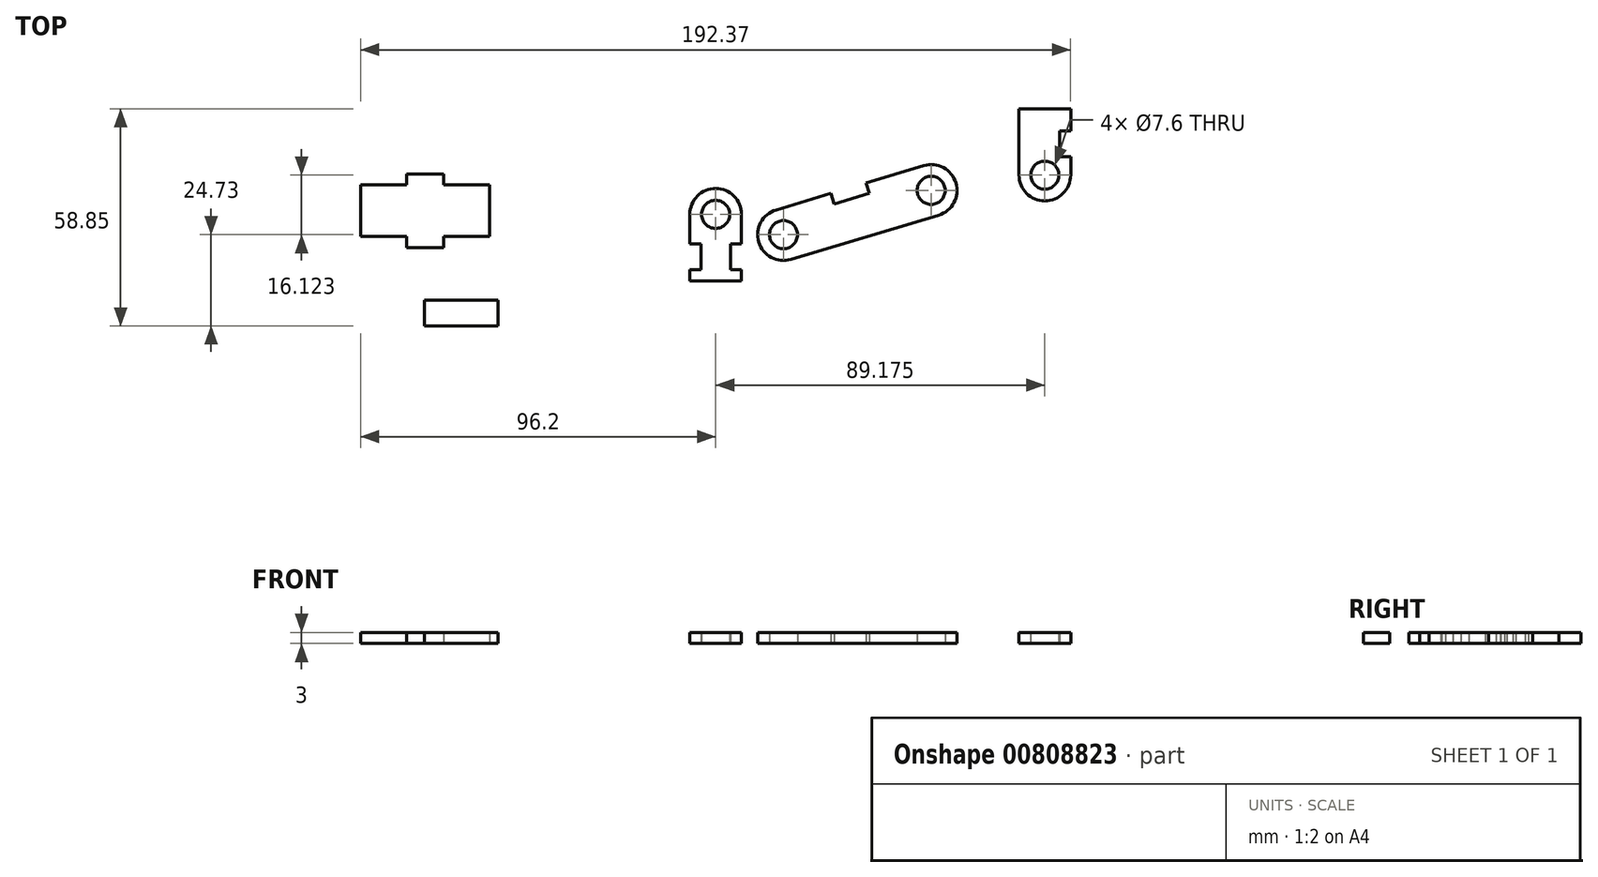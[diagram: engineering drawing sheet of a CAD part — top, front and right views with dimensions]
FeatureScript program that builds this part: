
annotation { "Feature Type Name" : "Feature", "Feature Type Description" : "" }
export const myFeature = defineFeature(function(context is Context, id is Id, definition is map)
    precondition{}
    {
        {
            var Q0;
            Q0=qCreatedBy(makeId("Top.planeOp"),FACE);
            var sketch = newSketch(context, id + "F0", { "sketchPlane" : qUnion([Q0])});
            skLineSegment(sketch, "E0.bottom", {"start": v(-7, 12.5) * mm, "end": v(7, 12.5) * mm});
            skLineSegment(sketch, "E0.top", {"start": v(-7, -12.5) * mm, "end": v(7, -12.5) * mm});
            skLineSegment(sketch, "E0.left", {"start": v(-7, 12.5) * mm, "end": v(-7, -12.5) * mm});
            skLineSegment(sketch, "E0.right", {"start": v(7, 12.5) * mm, "end": v(7, -12.5) * mm});
            skPoint(sketch, "E0.middle", {"position": v(0, 0) * mm});
            skCircle(sketch, "E1", {"center": v(0, 5.5) * mm, "radius": 7 * mm});
            skCircle(sketch, "E2", {"center": v(0, 5.5) * mm, "radius": 3.8 * mm});
            skLineSegment(sketch, "E3.bottom", {"start": v(-7, -9.5) * mm, "end": v(-4, -9.5) * mm});
            skLineSegment(sketch, "E3.top", {"start": v(-7, -2.5) * mm, "end": v(-4, -2.5) * mm});
            skLineSegment(sketch, "E3.left", {"start": v(-7, -9.5) * mm, "end": v(-7, -2.5) * mm});
            skLineSegment(sketch, "E3.right", {"start": v(-4, -9.5) * mm, "end": v(-4, -2.5) * mm});
            skLineSegment(sketch, "E4.bottom", {"start": v(7, -9.5) * mm, "end": v(4, -9.5) * mm});
            skLineSegment(sketch, "E4.top", {"start": v(7, -2.5) * mm, "end": v(4, -2.5) * mm});
            skLineSegment(sketch, "E4.left", {"start": v(7, -9.5) * mm, "end": v(7, -2.5) * mm});
            skLineSegment(sketch, "E4.right", {"start": v(4, -9.5) * mm, "end": v(4, -2.5) * mm});
            skSolve(sketch);
        }
        {
            var Q0;
            {var subQ7=sQuery(id+"F0.wireOp",EDGE,"E0.top");Q0=makeQuery(id+"F0.imprint","IMPRINT",FACE,{"disambiguationData":[TD([[makeQuery(id+"F0.imprint","IMPRINT",EDGE,{"derivedFrom":subQ7}),1.0]])]});}
            var Q1;
            Q1=makeQuery(id+"F0.imprint","IMPRINT",FACE,{"disambiguationData":[TD([[makeQuery(id+"F0.imprint","IMPRINT",EDGE,{"derivedFrom":sQuery(id+"F0.wireOp",EDGE,"E2")}),-1.0]])]});
            extrude(context, id + "F1", {"entities" : qUnion([Q0, Q1]), "depth" : 3 * mm, "offsetDistance" : 25 * mm});
        }
        {
            var Q0;
            Q0=qCreatedBy(makeId("Top.planeOp"),FACE);
            var sketch = newSketch(context, id + "F2", { "sketchPlane" : qUnion([Q0])});
            skLineSegment(sketch, "E5", {"start": v(18.38, 0) * mm, "end": v(58.38, 12) * mm});
            skCircle(sketch, "E6", {"center": v(18.38, 0) * mm, "radius": 7 * mm});
            skCircle(sketch, "E7", {"center": v(58.38, 12) * mm, "radius": 7 * mm});
            skCircle(sketch, "E8", {"center": v(58.38, 12) * mm, "radius": 3.8 * mm});
            skCircle(sketch, "E9", {"center": v(18.38, 0) * mm, "radius": 3.8 * mm});
            skLineSegment(sketch, "E10", {"start": v(16.37, 6.7) * mm, "end": v(56.37, 18.7) * mm});
            skLineSegment(sketch, "E11", {"start": v(60.4, 5.3) * mm, "end": v(20.4, -6.7) * mm});
            skLineSegment(sketch, "E12", {"start": v(31.21, 11.16) * mm, "end": v(32.08, 8.29) * mm});
            skLineSegment(sketch, "E13", {"start": v(32.08, 8.29) * mm, "end": v(41.65, 11.16) * mm});
            skLineSegment(sketch, "E14", {"start": v(41.65, 11.16) * mm, "end": v(40.8, 14.03) * mm});
            skSolve(sketch);
        }
        {
            var Q0;
            {var subQ5=sQuery(id+"F2.wireOp",EDGE,"E11");Q0=makeQuery(id+"F2.imprint","IMPRINT",FACE,{"disambiguationData":[TD([[makeQuery(id+"F2.imprint","IMPRINT",EDGE,{"derivedFrom":subQ5}),-1.0]])]});}
            var Q1;
            Q1=makeQuery(id+"F2.imprint","IMPRINT",FACE,{"disambiguationData":[TD([[makeQuery(id+"F2.imprint","IMPRINT",EDGE,{"derivedFrom":sQuery(id+"F2.wireOp",EDGE,"E9")}),-1.0]])]});
            var Q2;
            Q2=makeQuery(id+"F2.imprint","IMPRINT",FACE,{"disambiguationData":[TD([[makeQuery(id+"F2.imprint","IMPRINT",EDGE,{"derivedFrom":sQuery(id+"F2.wireOp",EDGE,"E8")}),-1.0]])]});
            var Q3;
            {var subQ3=sQuery(id+"F2.wireOp",EDGE,"E12");Q3=makeQuery(id+"F2.imprint","IMPRINT",FACE,{"disambiguationData":[TD([[makeQuery(id+"F2.imprint","IMPRINT",EDGE,{"derivedFrom":subQ3}),-1.0]])]});}
            extrude(context, id + "F3", {"entities" : qUnion([Q0, Q1, Q2, Q3]), "depth" : 3 * mm, "offsetDistance" : 25 * mm});
        }
        {
            var Q0;
            Q0=qCreatedBy(makeId("Top.planeOp"),FACE);
            var sketch = newSketch(context, id + "F4", { "sketchPlane" : qUnion([Q0])});
            skCircle(sketch, "E15", {"center": v(89.17, 16.12) * mm, "radius": 3.8 * mm});
            skLineSegment(sketch, "E16.bottom", {"start": v(96.17, -1.88) * mm, "end": v(82.17, -1.88) * mm});
            skLineSegment(sketch, "E16.top", {"start": v(96.17, 34.12) * mm, "end": v(82.17, 34.12) * mm});
            skLineSegment(sketch, "E16.left", {"start": v(96.17, -1.88) * mm, "end": v(96.17, 34.12) * mm});
            skLineSegment(sketch, "E16.right", {"start": v(82.17, -1.88) * mm, "end": v(82.17, 34.12) * mm});
            skCircle(sketch, "E17", {"center": v(89.17, 16.12) * mm, "radius": 7 * mm});
            skLineSegment(sketch, "E18.bottom", {"start": v(96.17, 28.12) * mm, "end": v(93.17, 28.12) * mm});
            skLineSegment(sketch, "E18.top", {"start": v(96.17, 21.12) * mm, "end": v(93.17, 21.12) * mm});
            skLineSegment(sketch, "E18.left", {"start": v(96.17, 28.12) * mm, "end": v(96.17, 21.12) * mm});
            skLineSegment(sketch, "E18.right", {"start": v(93.17, 28.12) * mm, "end": v(93.17, 21.12) * mm});
            skSolve(sketch);
        }
        {
            var Q0;
            {var subQ1=sQuery(id+"F4.wireOp",EDGE,"E16.left");var subQ3=sQuery(id+"F4.wireOp",EDGE,"E17");var subQ4=makeQuery(id+"F4.imprint","INTERSECT",VERTEX,{"derivedFrom":[subQ1,subQ3]});Q0=makeQuery(id+"F4.imprint","IMPRINT",FACE,{"disambiguationData":[TD([[makeQuery(id+"F4.imprint","IMPRINT",EDGE,{"disambiguationData":[TD([[subQ4,-1.0]])],"derivedFrom":subQ3}),-1.0]])]});}
            var Q1;
            Q1=makeQuery(id+"F4.imprint","IMPRINT",FACE,{"disambiguationData":[TD([[makeQuery(id+"F4.imprint","IMPRINT",EDGE,{"derivedFrom":sQuery(id+"F4.wireOp",EDGE,"E15")}),-1.0]])]});
            var Q2;
            {var subQ6=sQuery(id+"F4.wireOp",EDGE,"E16.top");Q2=makeQuery(id+"F4.imprint","IMPRINT",FACE,{"disambiguationData":[TD([[makeQuery(id+"F4.imprint","IMPRINT",EDGE,{"derivedFrom":subQ6}),1.0]])]});}
            extrude(context, id + "F5", {"entities" : qUnion([Q0, Q1, Q2]), "depth" : 3 * mm, "offsetDistance" : 25 * mm});
        }
        {
            var Q0;
            Q0=qCreatedBy(makeId("Top.planeOp"),FACE);
            var sketch = newSketch(context, id + "F6", { "sketchPlane" : qUnion([Q0])});
            skLineSegment(sketch, "E19.bottom", {"start": v(-58.94, -17.73) * mm, "end": v(-78.94, -17.73) * mm});
            skLineSegment(sketch, "E19.top", {"start": v(-58.94, -24.73) * mm, "end": v(-78.94, -24.73) * mm});
            skLineSegment(sketch, "E19.left", {"start": v(-58.94, -17.73) * mm, "end": v(-58.94, -24.73) * mm});
            skLineSegment(sketch, "E19.right", {"start": v(-78.94, -17.73) * mm, "end": v(-78.94, -24.73) * mm});
            skPoint(sketch, "E19.middle", {"position": v(-68.94, -21.23) * mm});
            skLineSegment(sketch, "E20.bottom", {"start": v(-61.2, -0.52) * mm, "end": v(-96.2, -0.52) * mm});
            skLineSegment(sketch, "E20.top", {"start": v(-61.2, 13.48) * mm, "end": v(-96.2, 13.48) * mm});
            skLineSegment(sketch, "E20.left", {"start": v(-61.2, -0.52) * mm, "end": v(-61.2, 13.48) * mm});
            skLineSegment(sketch, "E20.right", {"start": v(-96.2, -0.52) * mm, "end": v(-96.2, 13.48) * mm});
            skPoint(sketch, "E20.middle", {"position": v(-78.7, 6.48) * mm});
            skLineSegment(sketch, "E21.bottom", {"start": v(-73.7, -3.52) * mm, "end": v(-83.7, -3.52) * mm});
            skLineSegment(sketch, "E21.top", {"start": v(-73.7, 2.48) * mm, "end": v(-83.7, 2.48) * mm});
            skLineSegment(sketch, "E21.left", {"start": v(-73.7, -3.52) * mm, "end": v(-73.7, 2.48) * mm});
            skLineSegment(sketch, "E21.right", {"start": v(-83.7, -3.52) * mm, "end": v(-83.7, 2.48) * mm});
            skPoint(sketch, "E21.middle", {"position": v(-78.7, -0.52) * mm});
            skLineSegment(sketch, "E22.bottom", {"start": v(-73.7, 16.48) * mm, "end": v(-83.7, 16.48) * mm});
            skLineSegment(sketch, "E22.top", {"start": v(-73.7, 10.48) * mm, "end": v(-83.7, 10.48) * mm});
            skLineSegment(sketch, "E22.left", {"start": v(-73.7, 16.48) * mm, "end": v(-73.7, 10.48) * mm});
            skLineSegment(sketch, "E22.right", {"start": v(-83.7, 16.48) * mm, "end": v(-83.7, 10.48) * mm});
            skPoint(sketch, "E22.middle", {"position": v(-78.7, 13.48) * mm});
            skSolve(sketch);
        }
        {
            var Q0;
            Q0=makeQuery(id+"F6.imprint","IMPRINT",FACE,{"disambiguationData":[TD([[makeQuery(id+"F6.imprint","IMPRINT",EDGE,{"derivedFrom":sQuery(id+"F6.wireOp",EDGE,"E19.bottom")}),1.0]])]});
            var Q1;
            {var subQ3=sQuery(id+"F6.wireOp",EDGE,"E20.left");Q1=makeQuery(id+"F6.imprint","IMPRINT",FACE,{"disambiguationData":[TD([[makeQuery(id+"F6.imprint","IMPRINT",EDGE,{"derivedFrom":subQ3}),1.0]])]});}
            var Q2;
            {var subQ5=sQuery(id+"F6.wireOp",EDGE,"E21.top");Q2=makeQuery(id+"F6.imprint","IMPRINT",FACE,{"disambiguationData":[TD([[makeQuery(id+"F6.imprint","IMPRINT",EDGE,{"derivedFrom":subQ5}),1.0]])]});}
            var Q3;
            {var subQ5=sQuery(id+"F6.wireOp",EDGE,"E21.bottom");Q3=makeQuery(id+"F6.imprint","IMPRINT",FACE,{"disambiguationData":[TD([[makeQuery(id+"F6.imprint","IMPRINT",EDGE,{"derivedFrom":subQ5}),-1.0]])]});}
            var Q4;
            {var subQ5=sQuery(id+"F6.wireOp",EDGE,"E22.bottom");Q4=makeQuery(id+"F6.imprint","IMPRINT",FACE,{"disambiguationData":[TD([[makeQuery(id+"F6.imprint","IMPRINT",EDGE,{"derivedFrom":subQ5}),1.0]])]});}
            var Q5;
            {var subQ5=sQuery(id+"F6.wireOp",EDGE,"E22.top");Q5=makeQuery(id+"F6.imprint","IMPRINT",FACE,{"disambiguationData":[TD([[makeQuery(id+"F6.imprint","IMPRINT",EDGE,{"derivedFrom":subQ5}),-1.0]])]});}
            extrude(context, id + "F7", {"entities" : qUnion([Q0, Q1, Q2, Q3, Q4, Q5]), "depth" : 3 * mm, "offsetDistance" : 25 * mm});
        }
    });
